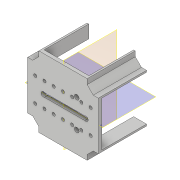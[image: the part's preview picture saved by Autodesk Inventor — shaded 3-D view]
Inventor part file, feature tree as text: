
AUTODESK INVENTOR PART (.ipt)
format: ipt  version: 2022 (Build 260153000, 153)  size: 265,728 bytes
history: native  units: mm
features: plane x9, sketch x6, extrude x5, other x5, projected_geometry x2, reference x2, hole x1, pattern_linear x1
ambient origin geometry x8: Origin, YZ Plane, XZ Plane, XY Plane, X Axis, Y Axis, Z Axis, Center Point
bodies: Body1 (feature_tree)
feature tree (31):
  plane  "Work Plane1"
  plane  "Work Plane2"
  plane  "Work Plane4"
  extrude  "Extrusion1"  Depth=24.9mm
  hole  "Hole1"  [1 undecoded]
  extrude  "IM_offset"  Depth=2.43mm TaperAngle=0.0deg
  extrude  "Extrusion6"  Depth=0.2mm
  plane  "Work Plane3"
  sketch  "Sketch9"  dims[d26=1.0mm d27=0.0mm d28=2.9mm]
  plane  "Work Plane5"
  extrude  "Extrusion9"  Depth=2.9mm
  plane  "Work Plane6"
  plane  "Work Plane7"
  plane  "Arbeitsebene8"
  plane  "Arbeitsebene9"
  extrude  "Extrusion12"  Depth=1.2mm
  pattern_linear  "Rechteckige Anordnung1"  Spacing1=31.5mm  [1 undecoded]
  sketch  "Sketch1"  dims[d0=45.0deg d2=24.9mm]
  sketch  "Sketch5"  dims[d3=3.14mm d4=26.9mm]
  sketch  "Skizze6"  dims[d5=20.0mm d6=2.43mm d7=0.0mm]
  projected_geometry  "Projizierte Kontur2"
  sketch  "Sketch7"  dims[d18=3.3mm d19=6.0mm d20=4.0mm d21=2.0mm d22=90.0deg d23=12.0mm d24=20.594885mm d25=0.2mm]
  sketch  "Skizze13"  dims[d29=10.0mm d30=0.0mm d44=1.2mm d49=31.5mm d50=0.0mm d55=2.2mm d56=2.2mm d57=8.5mm d58=8.5mm d59=31.5mm d60=0.0mm d61=70.0mm d63=6.5mm d64=1.2mm d65=40.0mm d67=360.0deg]
  projected_geometry  "Projizierte Kontur6"
  reference  "Referenz2"
  reference  "Referenz3"
  other  "Assembly_Cube_Z-Stage_NEMA11_china_v3.iam"
  other  "Assembly_Cube_empty_IM_v3:2"
  other  "10_Cube_1x1_IM:2"
  other  "Assembly_Cube_empty_IM_v3:1"
  other  "10_Cube_1x1_IM:1"
note: 2 required parameter values undecoded (feature->parameter linkage not recoverable at this tier; creation-order binding heuristic only, values carry confidence <= 0.55)
